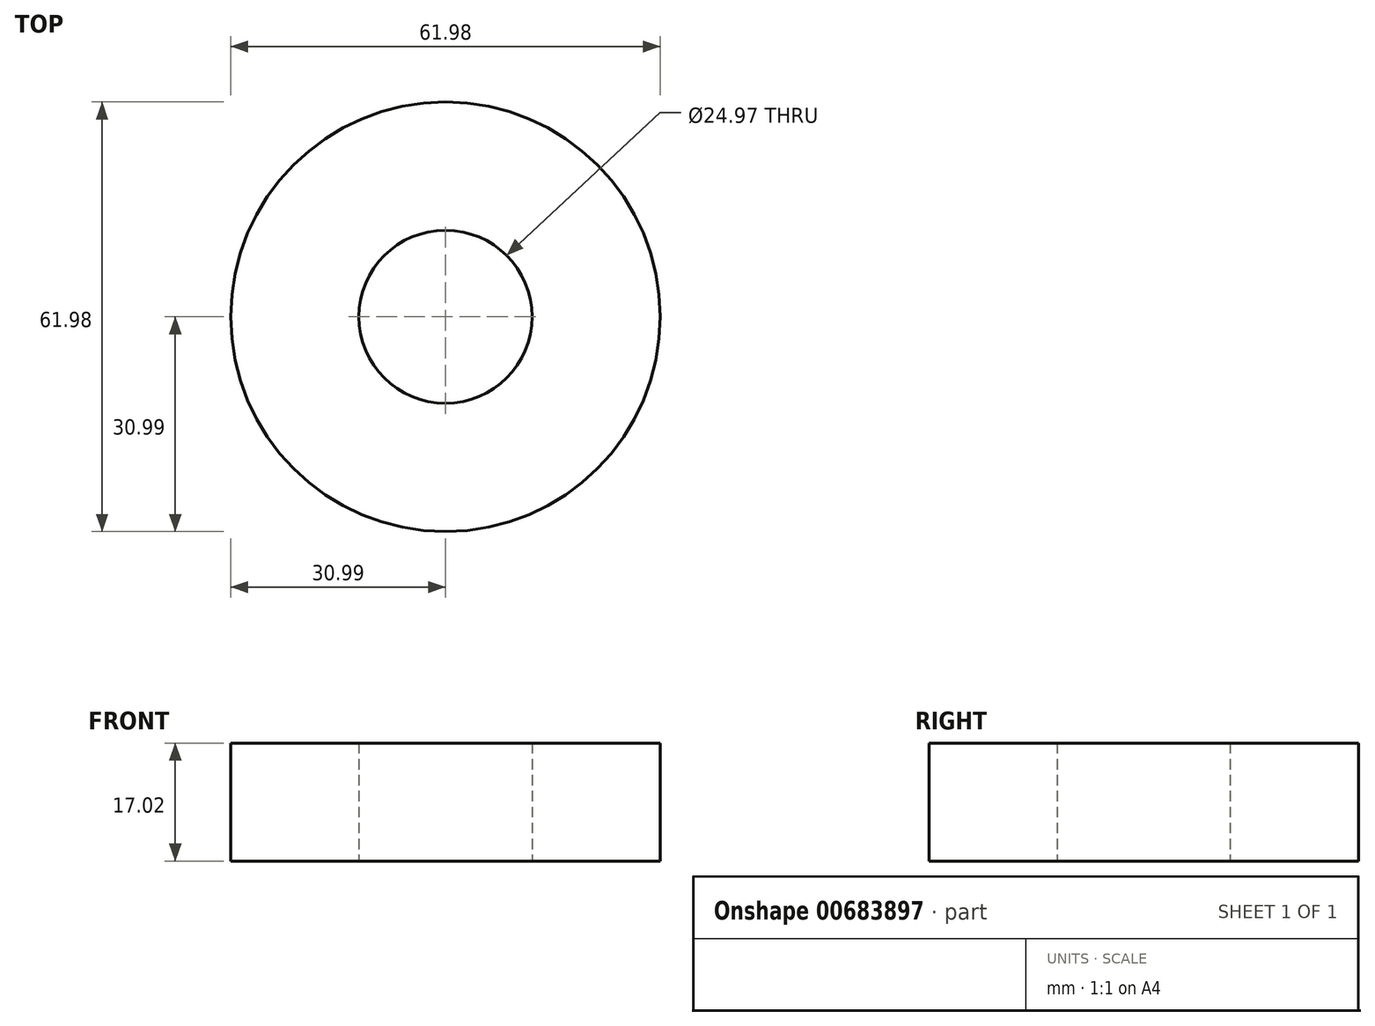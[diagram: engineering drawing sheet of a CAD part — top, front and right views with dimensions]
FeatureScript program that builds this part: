
annotation { "Feature Type Name" : "Feature", "Feature Type Description" : "" }
export const myFeature = defineFeature(function(context is Context, id is Id, definition is map)
    precondition{}
    {
        {
            var Q0;
            Q0=qCreatedBy(makeId("Top.planeOp"),FACE);
            var sketch = newSketch(context, id + "F0", { "sketchPlane" : qUnion([Q0])});
            skCircle(sketch, "E0", {"center": v(0, 0) * mm, "radius": 12.48 * mm});
            skCircle(sketch, "E1", {"center": v(0, 0) * mm, "radius": 30.99 * mm});
            skSolve(sketch);
        }
        {
            var Q0;
            Q0=makeQuery(id+"F0.imprint","IMPRINT",FACE,{"disambiguationData":[TD([[makeQuery(id+"F0.imprint","IMPRINT",EDGE,{"derivedFrom":sQuery(id+"F0.wireOp",EDGE,"E0")}),-1.0]])]});
            extrude(context, id + "F1", {"entities" : qUnion([Q0]), "depth" : 17.02 * mm, "offsetDistance" : 25.4 * mm});
        }
    });
